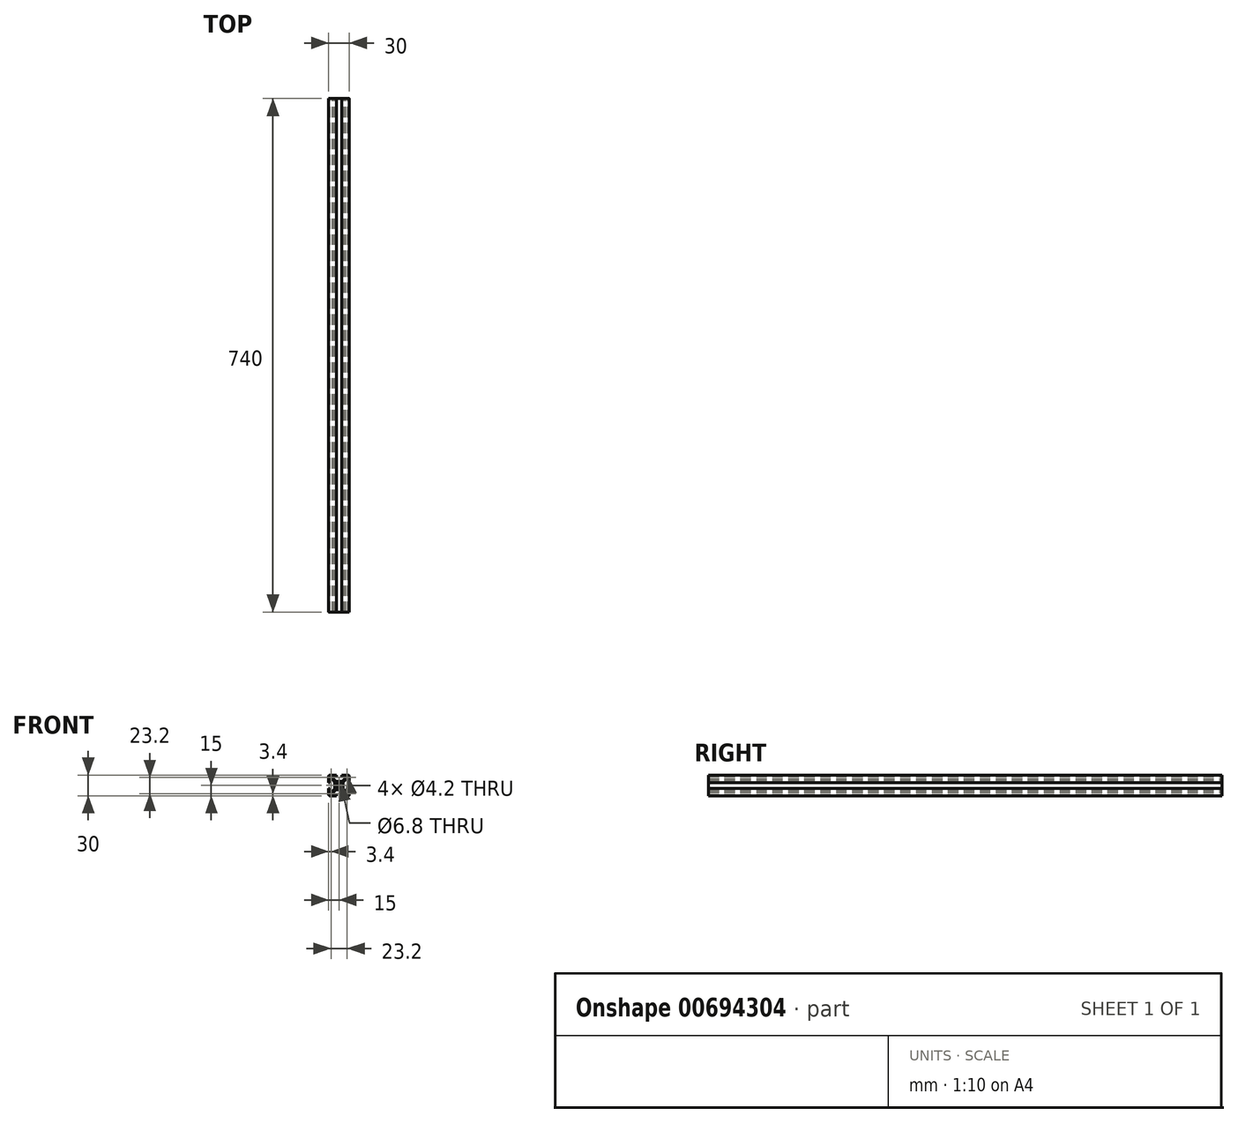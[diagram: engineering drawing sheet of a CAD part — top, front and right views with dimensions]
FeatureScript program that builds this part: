
annotation { "Feature Type Name" : "Feature", "Feature Type Description" : "" }
export const myFeature = defineFeature(function(context is Context, id is Id, definition is map)
    precondition{}
    {
        {
            var Q0;
            Q0=qCreatedBy(makeId("Front.planeOp"),FACE);
            var sketch = newSketch(context, id + "F0", { "sketchPlane" : qUnion([Q0])});
            skLineSegment(sketch, "E0", {"start": v(0, 6) * mm, "end": v(-4.59, 6) * mm});
            skLineSegment(sketch, "E1", {"start": v(-4.59, 6) * mm, "end": v(-8.25, 9.66) * mm});
            skLineSegment(sketch, "E2", {"start": v(-8.25, 9.66) * mm, "end": v(-8.25, 13) * mm});
            skLineSegment(sketch, "E3", {"start": v(-8.25, 13) * mm, "end": v(-4, 13) * mm});
            skLineSegment(sketch, "E4", {"start": v(-4, 13) * mm, "end": v(-4, 15) * mm});
            skLineSegment(sketch, "E5", {"start": v(-4, 15) * mm, "end": v(-13, 15) * mm});
            skLineSegment(sketch, "E6", {"start": v(-15, 13) * mm, "end": v(-15, 4) * mm});
            skLineSegment(sketch, "E7", {"start": v(-15, 4) * mm, "end": v(-13, 4) * mm});
            skLineSegment(sketch, "E8", {"start": v(-13, 4) * mm, "end": v(-13, 8.25) * mm});
            skLineSegment(sketch, "E9", {"start": v(-13, 8.25) * mm, "end": v(-9.66, 8.25) * mm});
            skLineSegment(sketch, "E10", {"start": v(-9.66, 8.25) * mm, "end": v(-6, 4.59) * mm});
            skLineSegment(sketch, "E11", {"start": v(-6, 4.59) * mm, "end": v(-6, 0) * mm});
            skLineSegment(sketch, "E12", {"start": v(-6, 0) * mm, "end": v(0, 0) * mm, "construction": true});
            skLineSegment(sketch, "E13", {"start": v(0, 0) * mm, "end": v(0, 6) * mm, "construction": true});
            skArc(sketch, "E14", {"start": v(0, 3.4) * mm, "mid": v(-2.4, 2.4) * mm, "end": v(-3.4, 0) * mm});
            skCircle(sketch, "E15", {"center": v(-11.6, 11.6) * mm, "radius": 2.1 * mm});
            skLineSegment(sketch, "E16", {"start": v(0, 0) * mm, "end": v(-7.38, 7.38) * mm, "construction": true});
            skLineSegment(sketch, "E17.1.0", {"start": v(-8.25, -13) * mm, "end": v(-8.25, -9.66) * mm});
            skLineSegment(sketch, "E17.1.1", {"start": v(-4, -15) * mm, "end": v(-4, -13) * mm});
            skLineSegment(sketch, "E17.1.2", {"start": v(-4, -13) * mm, "end": v(-8.25, -13) * mm});
            skLineSegment(sketch, "E17.1.3", {"start": v(-15, -4) * mm, "end": v(-15, -13) * mm});
            skLineSegment(sketch, "E17.1.4", {"start": v(-8.25, -9.66) * mm, "end": v(-4.59, -6) * mm});
            skLineSegment(sketch, "E17.1.5", {"start": v(-13, -15) * mm, "end": v(-4, -15) * mm});
            skLineSegment(sketch, "E17.1.6", {"start": v(-4.59, -6) * mm, "end": v(0, -6) * mm});
            skLineSegment(sketch, "E17.1.7", {"start": v(0, -6) * mm, "end": v(0, 0) * mm, "construction": true});
            skLineSegment(sketch, "E17.1.8", {"start": v(0, 0) * mm, "end": v(-6, 0) * mm, "construction": true});
            skLineSegment(sketch, "E17.1.9", {"start": v(-13, -4) * mm, "end": v(-15, -4) * mm});
            skLineSegment(sketch, "E17.1.10", {"start": v(-13, -8.25) * mm, "end": v(-13, -4) * mm});
            skArc(sketch, "E17.1.11", {"start": v(-3.4, 0) * mm, "mid": v(-2.4, -2.4) * mm, "end": v(0, -3.4) * mm});
            skLineSegment(sketch, "E17.1.12", {"start": v(-9.66, -8.25) * mm, "end": v(-13, -8.25) * mm});
            skLineSegment(sketch, "E17.1.13", {"start": v(0, 0) * mm, "end": v(-7.38, -7.38) * mm, "construction": true});
            skLineSegment(sketch, "E17.1.14", {"start": v(-6, -4.59) * mm, "end": v(-9.66, -8.25) * mm});
            skCircle(sketch, "E17.1.15", {"center": v(-11.6, -11.6) * mm, "radius": 2.1 * mm});
            skLineSegment(sketch, "E17.1.16", {"start": v(-6, 0) * mm, "end": v(-6, -4.59) * mm});
            skLineSegment(sketch, "E17.2.0", {"start": v(13, -8.25) * mm, "end": v(9.66, -8.25) * mm});
            skLineSegment(sketch, "E17.2.1", {"start": v(15, -4) * mm, "end": v(13, -4) * mm});
            skLineSegment(sketch, "E17.2.2", {"start": v(13, -4) * mm, "end": v(13, -8.25) * mm});
            skLineSegment(sketch, "E17.2.3", {"start": v(4, -15) * mm, "end": v(13, -15) * mm});
            skLineSegment(sketch, "E17.2.4", {"start": v(9.66, -8.25) * mm, "end": v(6, -4.59) * mm});
            skLineSegment(sketch, "E17.2.5", {"start": v(15, -13) * mm, "end": v(15, -4) * mm});
            skLineSegment(sketch, "E17.2.6", {"start": v(6, -4.59) * mm, "end": v(6, 0) * mm});
            skLineSegment(sketch, "E17.2.7", {"start": v(6, 0) * mm, "end": v(0, 0) * mm, "construction": true});
            skLineSegment(sketch, "E17.2.8", {"start": v(0, 0) * mm, "end": v(0, -6) * mm, "construction": true});
            skLineSegment(sketch, "E17.2.9", {"start": v(4, -13) * mm, "end": v(4, -15) * mm});
            skLineSegment(sketch, "E17.2.10", {"start": v(8.25, -13) * mm, "end": v(4, -13) * mm});
            skArc(sketch, "E17.2.11", {"start": v(0, -3.4) * mm, "mid": v(2.4, -2.4) * mm, "end": v(3.4, 0) * mm});
            skLineSegment(sketch, "E17.2.12", {"start": v(8.25, -9.66) * mm, "end": v(8.25, -13) * mm});
            skLineSegment(sketch, "E17.2.13", {"start": v(0, 0) * mm, "end": v(7.38, -7.38) * mm, "construction": true});
            skLineSegment(sketch, "E17.2.14", {"start": v(4.59, -6) * mm, "end": v(8.25, -9.66) * mm});
            skCircle(sketch, "E17.2.15", {"center": v(11.6, -11.6) * mm, "radius": 2.1 * mm});
            skLineSegment(sketch, "E17.2.16", {"start": v(0, -6) * mm, "end": v(4.59, -6) * mm});
            skLineSegment(sketch, "E17.3.0", {"start": v(8.25, 13) * mm, "end": v(8.25, 9.66) * mm});
            skLineSegment(sketch, "E17.3.1", {"start": v(4, 15) * mm, "end": v(4, 13) * mm});
            skLineSegment(sketch, "E17.3.2", {"start": v(4, 13) * mm, "end": v(8.25, 13) * mm});
            skLineSegment(sketch, "E17.3.3", {"start": v(15, 4) * mm, "end": v(15, 13) * mm});
            skLineSegment(sketch, "E17.3.4", {"start": v(8.25, 9.66) * mm, "end": v(4.59, 6) * mm});
            skLineSegment(sketch, "E17.3.5", {"start": v(13, 15) * mm, "end": v(4, 15) * mm});
            skLineSegment(sketch, "E17.3.6", {"start": v(4.59, 6) * mm, "end": v(0, 6) * mm});
            skLineSegment(sketch, "E17.3.7", {"start": v(0, 6) * mm, "end": v(0, 0) * mm, "construction": true});
            skLineSegment(sketch, "E17.3.8", {"start": v(0, 0) * mm, "end": v(6, 0) * mm, "construction": true});
            skLineSegment(sketch, "E17.3.9", {"start": v(13, 4) * mm, "end": v(15, 4) * mm});
            skLineSegment(sketch, "E17.3.10", {"start": v(13, 8.25) * mm, "end": v(13, 4) * mm});
            skArc(sketch, "E17.3.11", {"start": v(3.4, 0) * mm, "mid": v(2.4, 2.4) * mm, "end": v(0, 3.4) * mm});
            skLineSegment(sketch, "E17.3.12", {"start": v(9.66, 8.25) * mm, "end": v(13, 8.25) * mm});
            skLineSegment(sketch, "E17.3.13", {"start": v(0, 0) * mm, "end": v(7.38, 7.38) * mm, "construction": true});
            skLineSegment(sketch, "E17.3.14", {"start": v(6, 4.59) * mm, "end": v(9.66, 8.25) * mm});
            skCircle(sketch, "E17.3.15", {"center": v(11.6, 11.6) * mm, "radius": 2.1 * mm});
            skLineSegment(sketch, "E17.3.16", {"start": v(6, 0) * mm, "end": v(6, 4.59) * mm});
            skPoint(sketch, "E18.visualSharp", {"position": v(-15, 15) * mm});
            skArc(sketch, "E18.filletArc", {"start": v(-13, 15) * mm, "mid": v(-14.41, 14.41) * mm, "end": v(-15, 13) * mm});
            skPoint(sketch, "E19.visualSharp", {"position": v(15, 15) * mm});
            skArc(sketch, "E19.filletArc", {"start": v(15, 13) * mm, "mid": v(14.41, 14.41) * mm, "end": v(13, 15) * mm});
            skPoint(sketch, "E20.visualSharp", {"position": v(15, -15) * mm});
            skArc(sketch, "E20.filletArc", {"start": v(13, -15) * mm, "mid": v(14.41, -14.41) * mm, "end": v(15, -13) * mm});
            skPoint(sketch, "E21.visualSharp", {"position": v(-15, -15) * mm});
            skArc(sketch, "E21.filletArc", {"start": v(-15, -13) * mm, "mid": v(-14.41, -14.41) * mm, "end": v(-13, -15) * mm});
            skSolve(sketch);
        }
        {
            var Q0;
            Q0=qSketchRegion(id+"F0",true);
            extrude(context, id + "F1", {"entities" : qUnion([Q0]), "depth" : 740 * mm, "offsetDistance" : 25 * mm});
        }
    });
